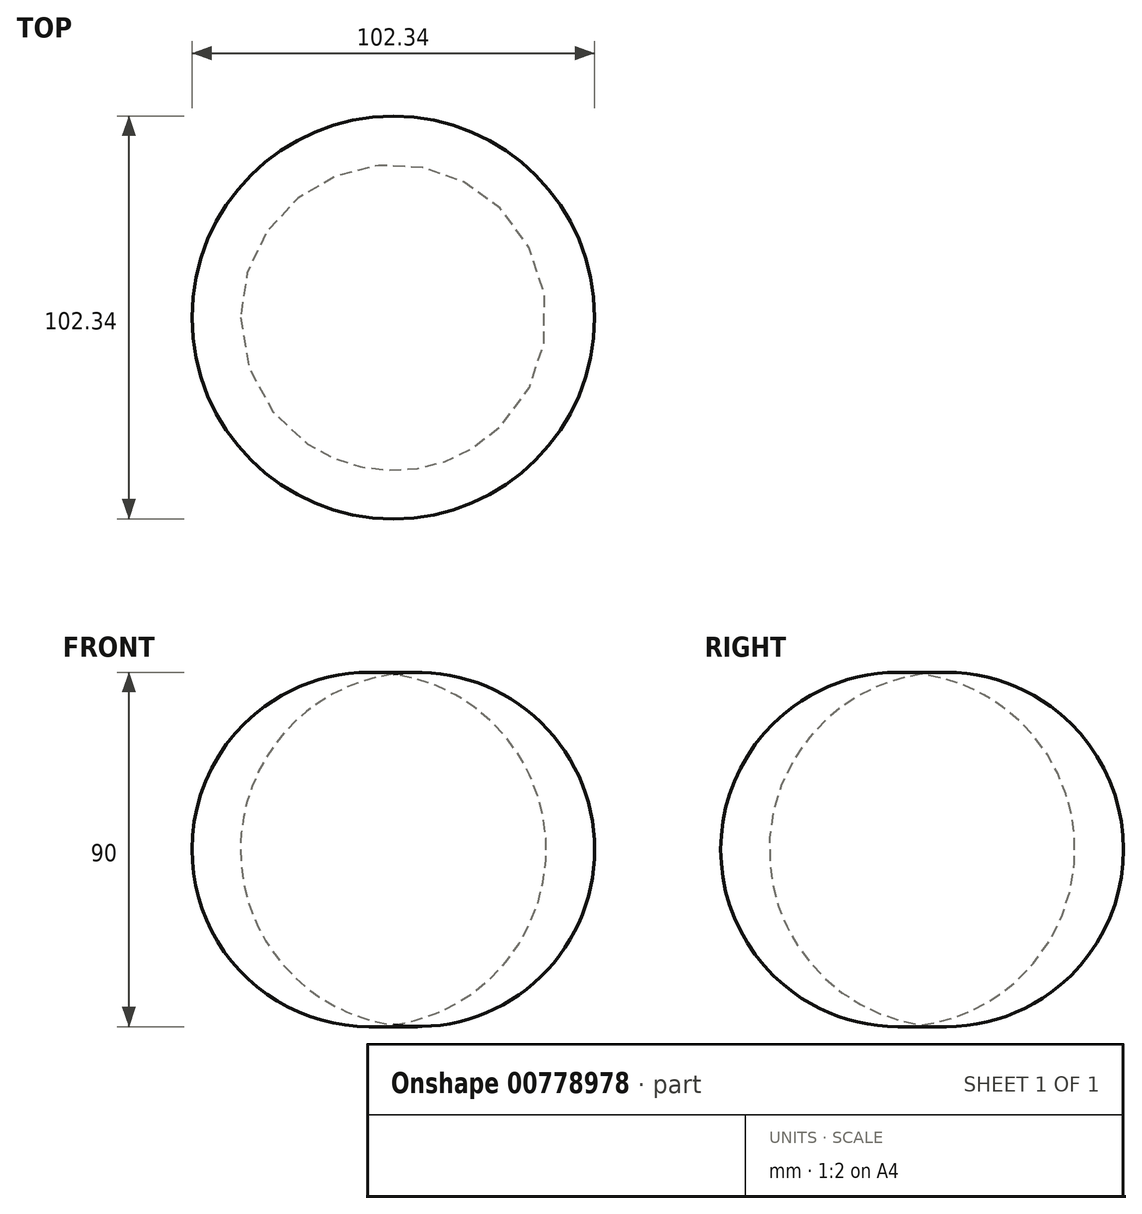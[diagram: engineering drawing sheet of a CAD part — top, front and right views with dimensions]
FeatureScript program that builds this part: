
annotation { "Feature Type Name" : "Feature", "Feature Type Description" : "" }
export const myFeature = defineFeature(function(context is Context, id is Id, definition is map)
    precondition{}
    {
        {
            var Q0;
            Q0=qCreatedBy(makeId("Front.planeOp"),FACE);
            var sketch = newSketch(context, id + "F0", { "sketchPlane" : qUnion([Q0])});
            skLineSegment(sketch, "E0", {"start": v(0, 96.44) * mm, "end": v(0, -91.84) * mm, "construction": true});
            skArc(sketch, "E1", {"start": v(0, 50) * mm, "mid": v(-38.83, 5.42) * mm, "end": v(0, -39.15) * mm});
            skLineSegment(sketch, "E2", {"start": v(0, 50) * mm, "end": v(0, -39.15) * mm});
            skSolve(sketch);
        }
        {
            var Q0;
            Q0 = qSketchRegion(id + "F0", true);
            var Q1;
            Q1=sQuery(id+"F0.wireOp",EDGE,"E0");
            revolve(context, id + "F1", {"surfaceOperationType" : NewSurfaceOperationType.NEW, "entities" : qUnion([Q0]), "axis" : qUnion([Q1]), "revolveType" : RevolveType.FULL});
        }
    });
